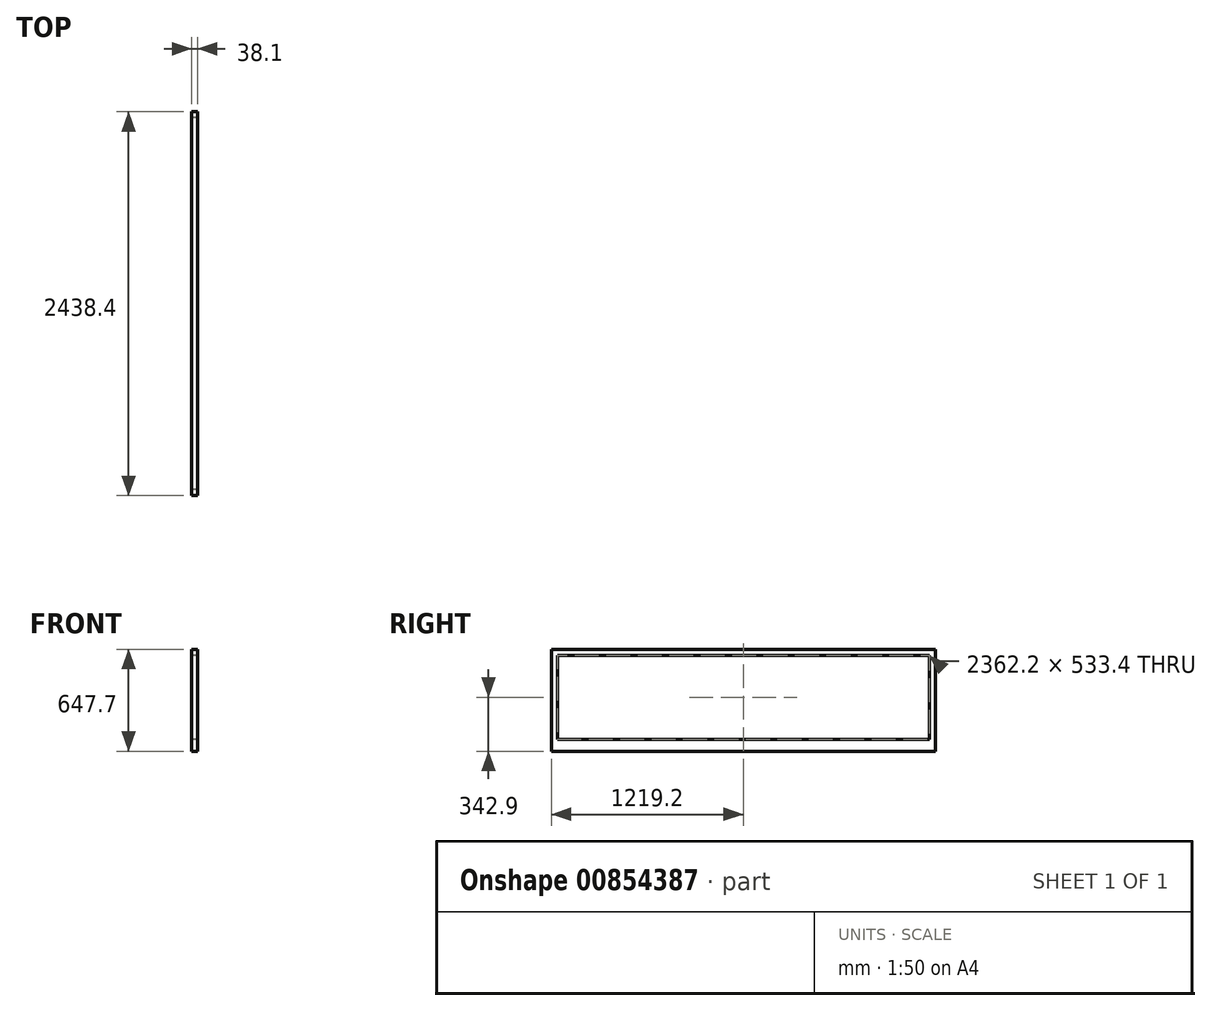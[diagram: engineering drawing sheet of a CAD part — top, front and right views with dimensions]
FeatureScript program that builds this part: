
annotation { "Feature Type Name" : "Feature", "Feature Type Description" : "" }
export const myFeature = defineFeature(function(context is Context, id is Id, definition is map)
    precondition{}
    {
        {
            var Q0;
            Q0=qCreatedBy(makeId("Top.planeOp"),FACE);
            var sketch = newSketch(context, id + "F0", { "sketchPlane" : qUnion([Q0])});
            skLineSegment(sketch, "E0.bottom", {"start": v(0, 0) * mm, "end": v(-38.1, 0) * mm});
            skLineSegment(sketch, "E0.top", {"start": v(0, 38.1) * mm, "end": v(-38.1, 38.1) * mm});
            skLineSegment(sketch, "E0.left", {"start": v(0, 0) * mm, "end": v(0, 38.1) * mm});
            skLineSegment(sketch, "E0.right", {"start": v(-38.1, 0) * mm, "end": v(-38.1, 38.1) * mm});
            skSolve(sketch);
        }
        {
            var Q0;
            Q0=makeQuery(id+"F0.imprint","IMPRINT",FACE,{"disambiguationData":[TD([[makeQuery(id+"F0.imprint","IMPRINT",EDGE,{"derivedFrom":sQuery(id+"F0.wireOp",EDGE,"E0.bottom")}),-1.0]])]});
            extrude(context, id + "F1", {"entities" : qUnion([Q0]), "depth" : 609.6 * mm, "offsetDistance" : 25.4 * mm});
        }
        {
            var Q0;
            Q0=makeQuery(id+"F1.opExtrude","SWEPT_FACE",FACE,{"disambiguationData":[OSD([sQuery(id+"F0.wireOp",EDGE,"E0.top")])]});
            var sketch = newSketch(context, id + "F2", { "sketchPlane" : qUnion([Q0])});
            skLineSegment(sketch, "E1.bottom", {"start": v(0, 0) * mm, "end": v(38.1, 0) * mm});
            skLineSegment(sketch, "E1.top", {"start": v(0, 76.2) * mm, "end": v(38.1, 76.2) * mm});
            skLineSegment(sketch, "E1.left", {"start": v(0, 0) * mm, "end": v(0, 76.2) * mm});
            skLineSegment(sketch, "E1.right", {"start": v(38.1, 0) * mm, "end": v(38.1, 76.2) * mm});
            skSolve(sketch);
        }
        {
            var Q0;
            Q0=makeQuery(id+"F2.imprint","IMPRINT",FACE,{"disambiguationData":[TD([[makeQuery(id+"F2.imprint","IMPRINT",EDGE,{"derivedFrom":sQuery(id+"F2.wireOp",EDGE,"E1.bottom")}),1.0]])]});
            extrude(context, id + "F3", {"entities" : qUnion([Q0]), "depth" : 2362.2 * mm, "offsetDistance" : 25.4 * mm});
        }
        {
            var Q0;
            Q0=makeQuery(id+"F3.opExtrude","CAP_FACE",FACE,{"disambiguationData":[OSD([sQuery(id+"F2.wireOp",EDGE,"E1.bottom"),sQuery(id+"F2.wireOp",EDGE,"E1.top"),sQuery(id+"F2.wireOp",EDGE,"E1.left"),sQuery(id+"F2.wireOp",EDGE,"E1.right")])],"isStart":false});
            var sketch = newSketch(context, id + "F4", { "sketchPlane" : qUnion([Q0])});
            skLineSegment(sketch, "E2.bottom", {"start": v(0, 0) * mm, "end": v(38.1, 0) * mm});
            skLineSegment(sketch, "E2.top", {"start": v(0, 76.2) * mm, "end": v(38.1, 76.2) * mm});
            skLineSegment(sketch, "E2.left", {"start": v(0, 0) * mm, "end": v(0, 76.2) * mm});
            skLineSegment(sketch, "E2.right", {"start": v(38.1, 0) * mm, "end": v(38.1, 76.2) * mm});
            skSolve(sketch);
        }
        {
            var Q0;
            Q0 = qSketchRegion(id + "F4", true);
            extrude(context, id + "F5", {"entities" : qUnion([Q0]), "depth" : 38.1 * mm, "offsetDistance" : 25.4 * mm});
        }
        {
            var Q0;
            Q0=makeQuery(id+"F5.opExtrude","SWEPT_FACE",FACE,{"disambiguationData":[OSD([sQuery(id+"F4.wireOp",EDGE,"E2.top")])]});
            extrude(context, id + "F6", {"entities" : qUnion([Q0]), "operationType" : NewBodyOperationType.ADD, "depth" : 533.4 * mm, "offsetDistance" : 25.4 * mm});
        }
        {
            var Q0;
            Q0=makeQuery(id+"F6.opExtrude","CAP_FACE",FACE,{"disambiguationData":[OSD([sQuery(id+"F4.wireOp",EDGE,"E2.top")])],"isStart":false});
            extrude(context, id + "F7", {"entities" : qUnion([Q0]), "depth" : 38.1 * mm, "offsetDistance" : 25.4 * mm});
        }
        {
            var Q0;
            {var subQ0=sQuery(id+"F4.wireOp",EDGE,"E2.top");Q0=makeQuery(id+"F7.opExtrude","SWEPT_FACE",FACE,{"disambiguationData":[OSD([subQ0]),TDD([makeQuery(id+"F6.opExtrude","CAP_EDGE",EDGE,{"disambiguationData":[OSD([subQ0]),TDD([makeQuery(id+"F5.opExtrude","CAP_EDGE",EDGE,{"disambiguationData":[OSD([subQ0])],"isStart":true})])],"isStart":false})])]});}
            extrude(context, id + "F8", {"entities" : qUnion([Q0]), "operationType" : NewBodyOperationType.ADD, "depth" : 2400.3 * mm, "offsetDistance" : 25.4 * mm});
        }
    });
